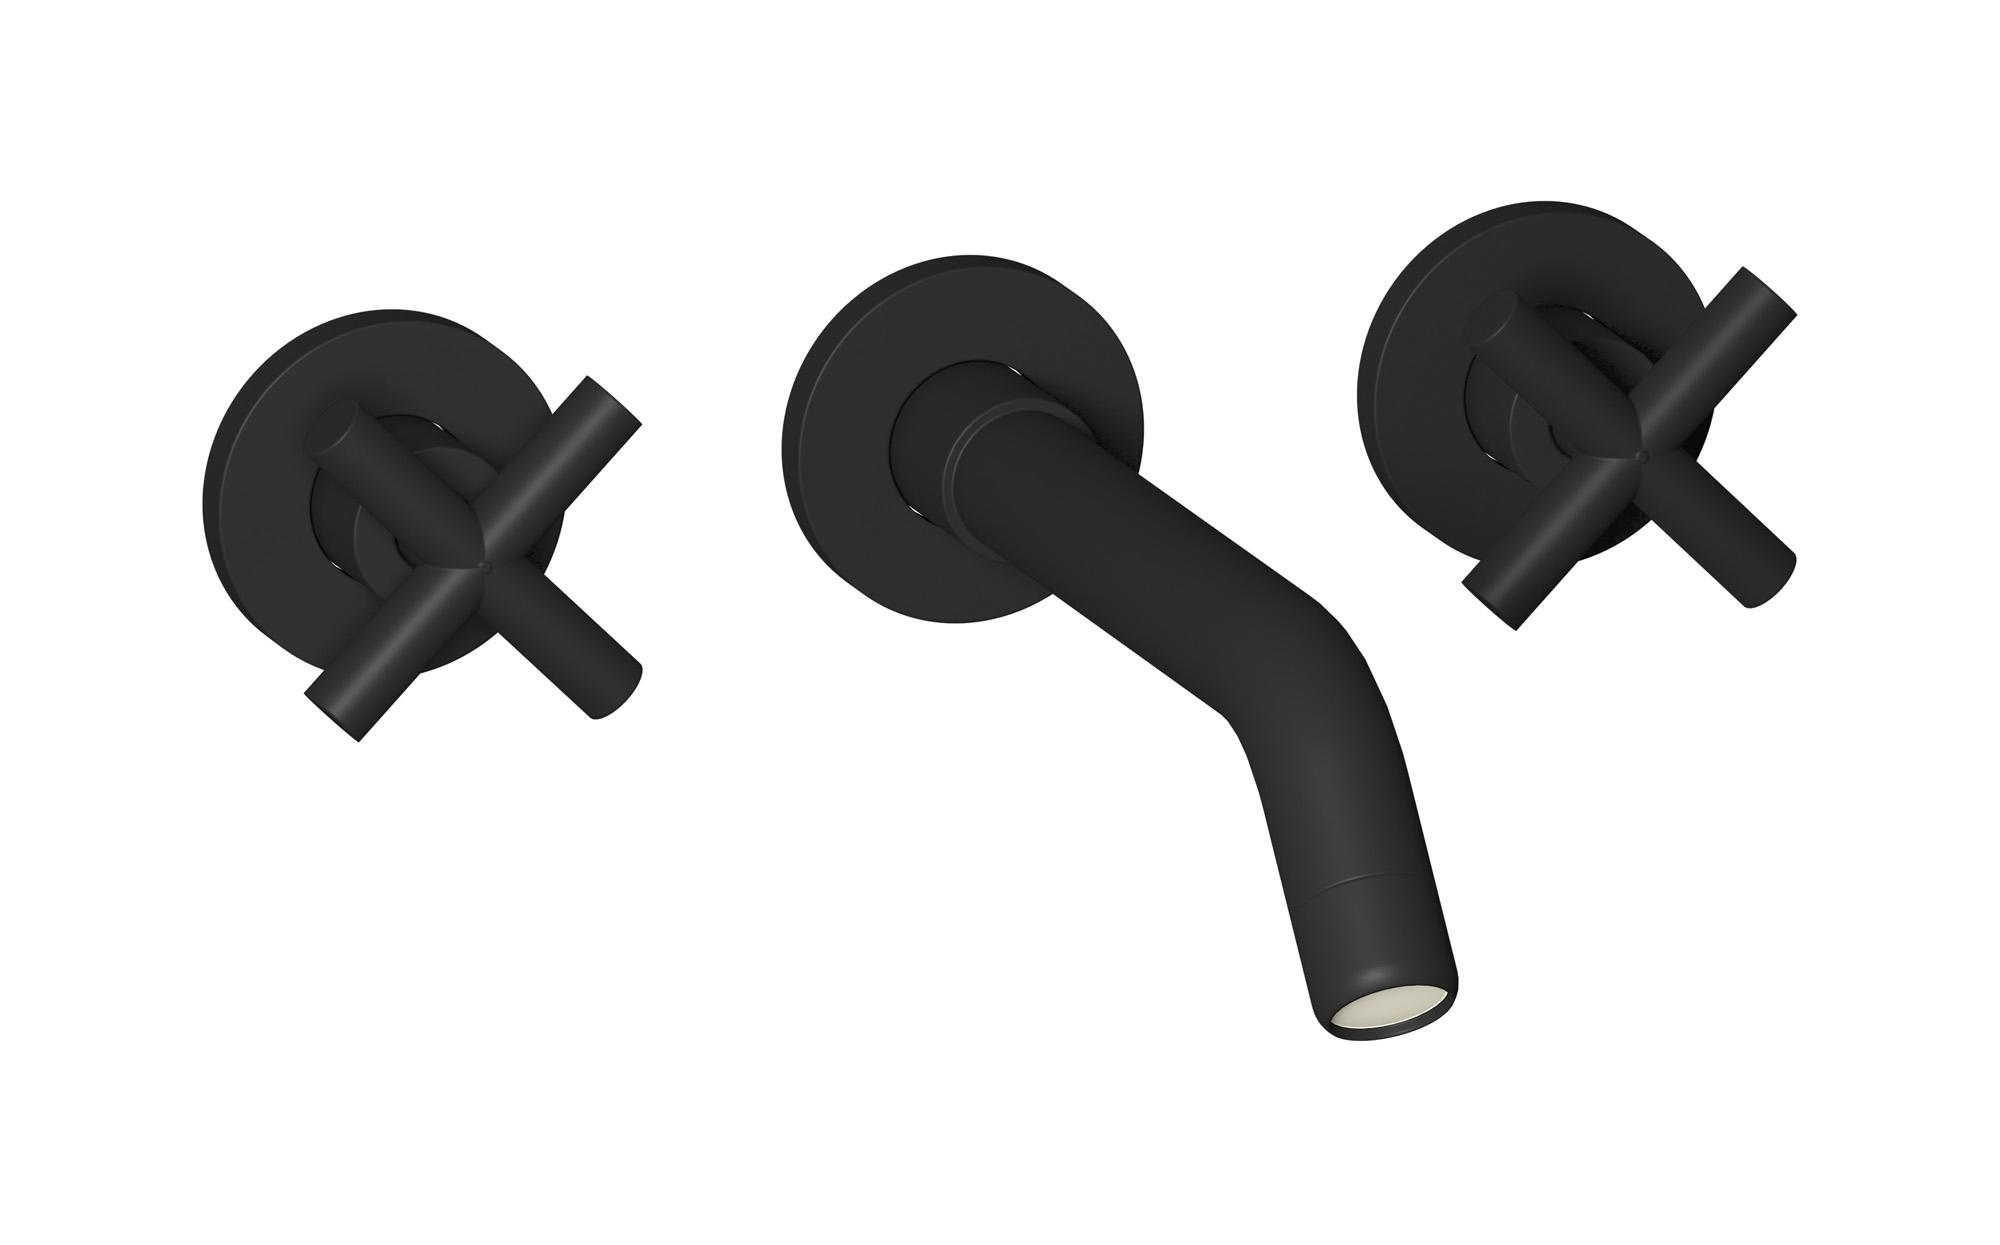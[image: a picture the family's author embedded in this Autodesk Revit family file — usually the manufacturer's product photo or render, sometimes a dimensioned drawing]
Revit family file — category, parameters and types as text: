
# Revit family: WO306
name_source: partatom
category: Apparecchi idraulici
units: mm (PartAtom-declared; Revit-internal decimal feet)

## family parameters
Basato su piano di lavoro = No
Condiviso = No
Mantieni orientamento annotazione = No
Numero OmniClass = 23.45.55.17
Punto di calcolo locali = No
Quota connettore circolare = Usa diametro
Sempre verticale = Sì
Taglio con vuoti quando caricato = No
Tipo di parte = Normale
Titolo OmniClass = Mixing Faucets

## types (5) — shared parameters
Cold water inlet = 10 mm  [stored 0.0328084 ft]
Commenti sul tipo = Lavatory faucet
Connessione CW = No
Connessione HW = No
Connessione di scarico = No
Connessione di ventilazione = No
Descrizione = Wall mounted widespread lavatory faucet
Hot water inlet = 10 mm  [stored 0.0328084 ft]
Produttore = IB Rubinetterie S.p.A.
URL = https://www.weareib.it
zero-valued in all types: Prospetto di default

## per-type parameters (varying)
| type | Finishes surface | Immagine tipo | Modello |
| Chrome | IB_Chrome | WO306CC.jpg | WO306CC |
| Brushed nickel | IB_Brushed nickel | WO306SS.jpg | WO306SS |
| Matt black | IB_matt black | WO306NP.jpg | WO306NP |
| Matt white | IB_matt white | WO306BO.jpg | WO306BO |
| Gold | IB_gold | WO306OO.jpg | WO306OO |

note: [stored X ft] marks values corroborated as IEEE doubles in the binary element streams (Revit-internal decimal feet)
